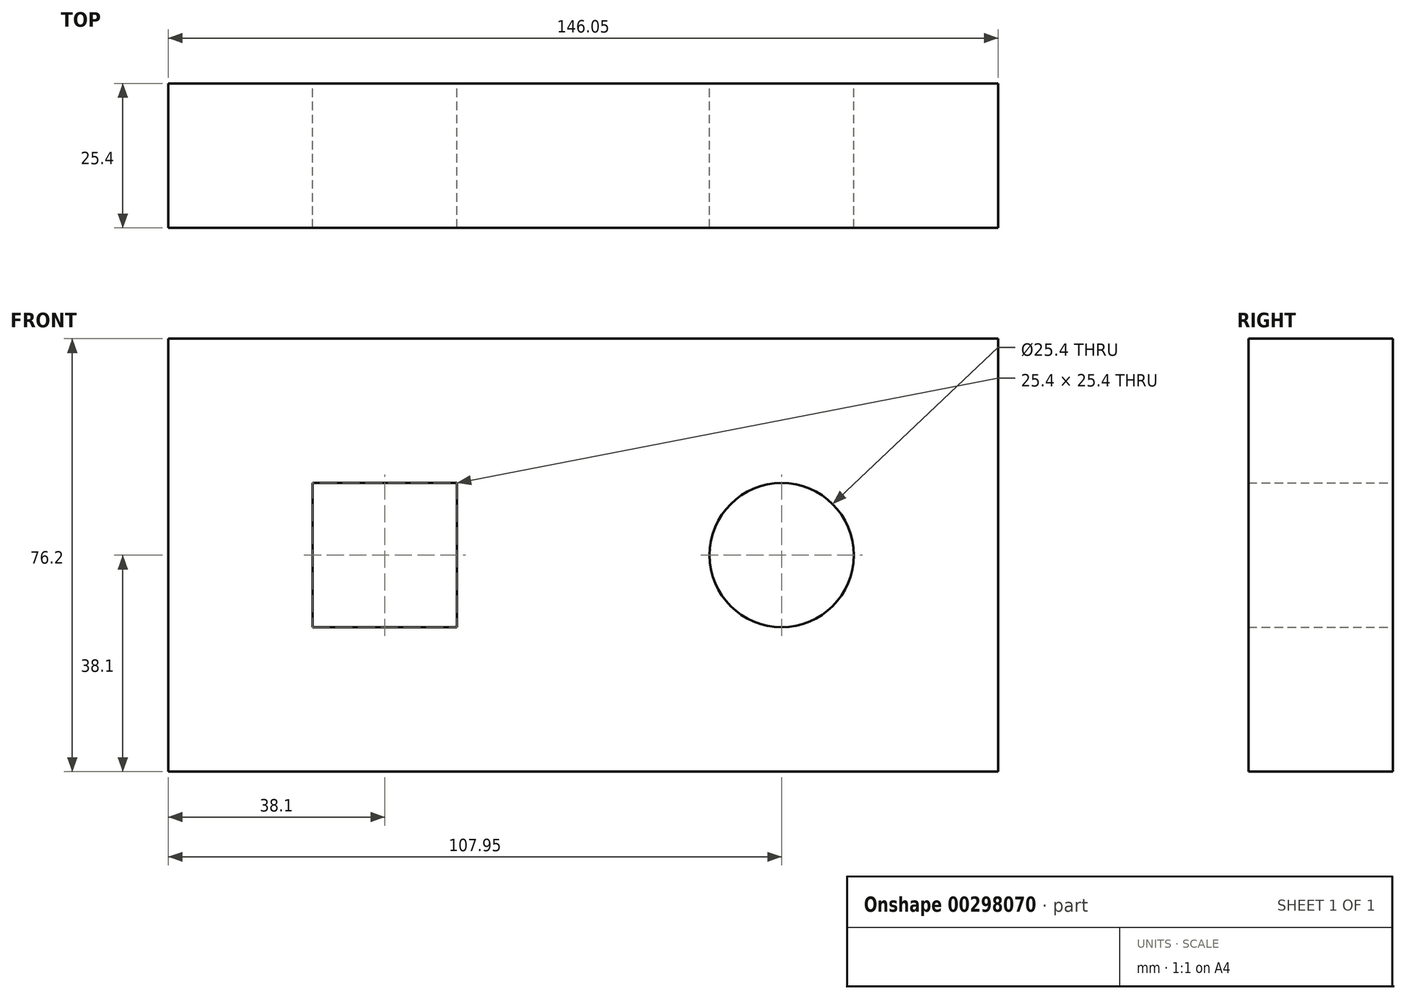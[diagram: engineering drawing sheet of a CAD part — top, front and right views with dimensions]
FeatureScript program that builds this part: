
annotation { "Feature Type Name" : "Feature", "Feature Type Description" : "" }
export const myFeature = defineFeature(function(context is Context, id is Id, definition is map)
    precondition{}
    {
        {
            var Q0;
            Q0=qCreatedBy(makeId("Front.planeOp"),FACE);
            var sketch = newSketch(context, id + "F0", { "sketchPlane" : qUnion([Q0])});
            skLineSegment(sketch, "E0.bottom", {"start": v(0, 0) * mm, "end": v(-146.05, 0) * mm});
            skLineSegment(sketch, "E0.top", {"start": v(0, 76.2) * mm, "end": v(-146.05, 76.2) * mm});
            skLineSegment(sketch, "E0.left", {"start": v(0, 0) * mm, "end": v(0, 76.2) * mm});
            skLineSegment(sketch, "E0.right", {"start": v(-146.05, 0) * mm, "end": v(-146.05, 76.2) * mm});
            skCircle(sketch, "E1", {"center": v(-38.1, 38.1) * mm, "radius": 12.7 * mm});
            skLineSegment(sketch, "E2.bottom", {"start": v(-120.65, 25.4) * mm, "end": v(-95.25, 25.4) * mm});
            skLineSegment(sketch, "E2.top", {"start": v(-120.65, 50.8) * mm, "end": v(-95.25, 50.8) * mm});
            skLineSegment(sketch, "E2.left", {"start": v(-120.65, 25.4) * mm, "end": v(-120.65, 50.8) * mm});
            skLineSegment(sketch, "E2.right", {"start": v(-95.25, 25.4) * mm, "end": v(-95.25, 50.8) * mm});
            skSolve(sketch);
        }
        {
            var Q0;
            Q0 = qSketchRegion(id + "F0", true);
            extrude(context, id + "F1", {"entities" : qUnion([Q0]), "depth" : 25.4 * mm});
        }
    });
